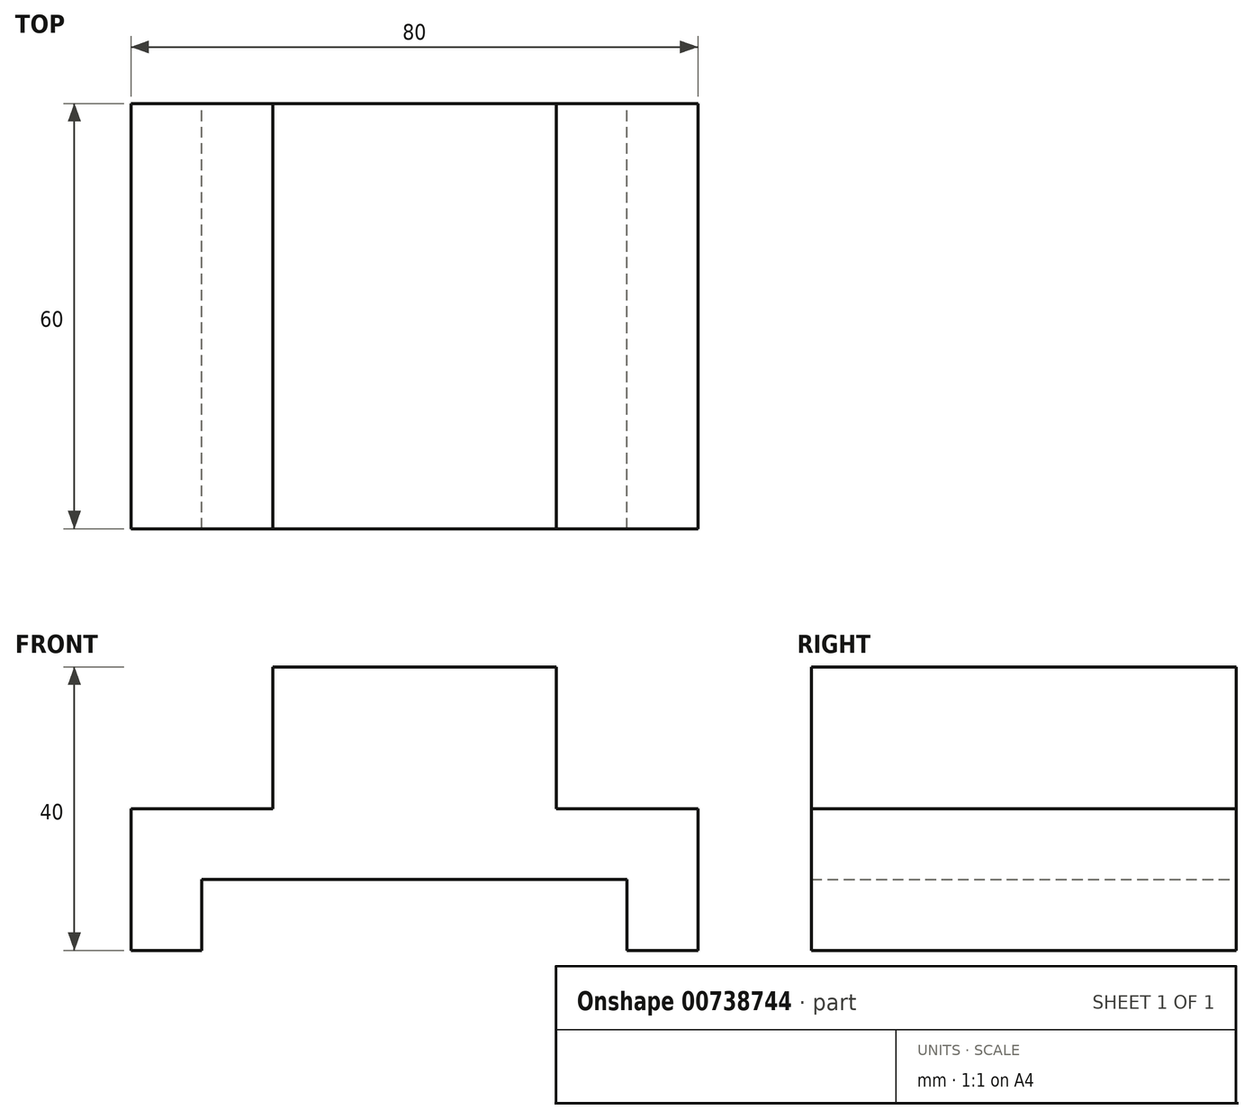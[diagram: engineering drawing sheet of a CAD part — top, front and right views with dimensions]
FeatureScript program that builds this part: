
annotation { "Feature Type Name" : "Feature", "Feature Type Description" : "" }
export const myFeature = defineFeature(function(context is Context, id is Id, definition is map)
    precondition{}
    {
        {
            var Q0;
            Q0=qCreatedBy(makeId("Front.planeOp"),FACE);
            var sketch = newSketch(context, id + "F0", { "sketchPlane" : qUnion([Q0])});
            skLineSegment(sketch, "E0", {"start": v(0, 0) * mm, "end": v(10, 0) * mm});
            skLineSegment(sketch, "E1", {"start": v(10, 0) * mm, "end": v(10, 10) * mm});
            skLineSegment(sketch, "E2", {"start": v(70, 10) * mm, "end": v(70, 0) * mm});
            skLineSegment(sketch, "E3", {"start": v(70, 0) * mm, "end": v(80, 0) * mm});
            skLineSegment(sketch, "E4", {"start": v(80, 0) * mm, "end": v(80, 20) * mm});
            skLineSegment(sketch, "E5", {"start": v(80, 20) * mm, "end": v(60, 20) * mm});
            skLineSegment(sketch, "E6", {"start": v(60, 20) * mm, "end": v(60, 40) * mm});
            skLineSegment(sketch, "E7", {"start": v(60, 40) * mm, "end": v(20, 40) * mm});
            skLineSegment(sketch, "E8", {"start": v(20, 40) * mm, "end": v(20, 20) * mm});
            skLineSegment(sketch, "E9", {"start": v(20, 20) * mm, "end": v(0, 20) * mm});
            skLineSegment(sketch, "E10", {"start": v(0, 20) * mm, "end": v(0, 0) * mm});
            skLineSegment(sketch, "E11", {"start": v(10, 10) * mm, "end": v(70, 10) * mm});
            skSolve(sketch);
        }
        {
            var Q0;
            Q0 = qSketchRegion(id + "F0", true);
            extrude(context, id + "F1", {"entities" : qUnion([Q0]), "depth" : 60 * mm, "offsetDistance" : 25 * mm});
        }
    });
